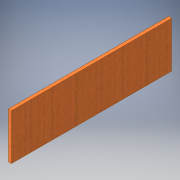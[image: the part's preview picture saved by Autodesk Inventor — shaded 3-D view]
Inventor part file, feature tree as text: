
AUTODESK INVENTOR PART (.ipt)
format: ipt  version: 2016 (Build 200138000, 138)  size: 102,400 bytes
history: native  units: in
note: dims shown in document units (in); Inventor stores cm internally (conversion verified against a paired STEP export)
features: extrude x1, sketch x1
ambient origin geometry x8: Origin, YZ Plane, XZ Plane, XY Plane, X Axis, Y Axis, Z Axis, Center Point
bodies: Solid1 (feature_tree)
feature tree (2):
  extrude  "Extrusion1"  Depth=6.5in
  sketch  "Sketch1"  dims[d0=22.75in d1=6.5in d2=0.4375in d3=0.0in]
